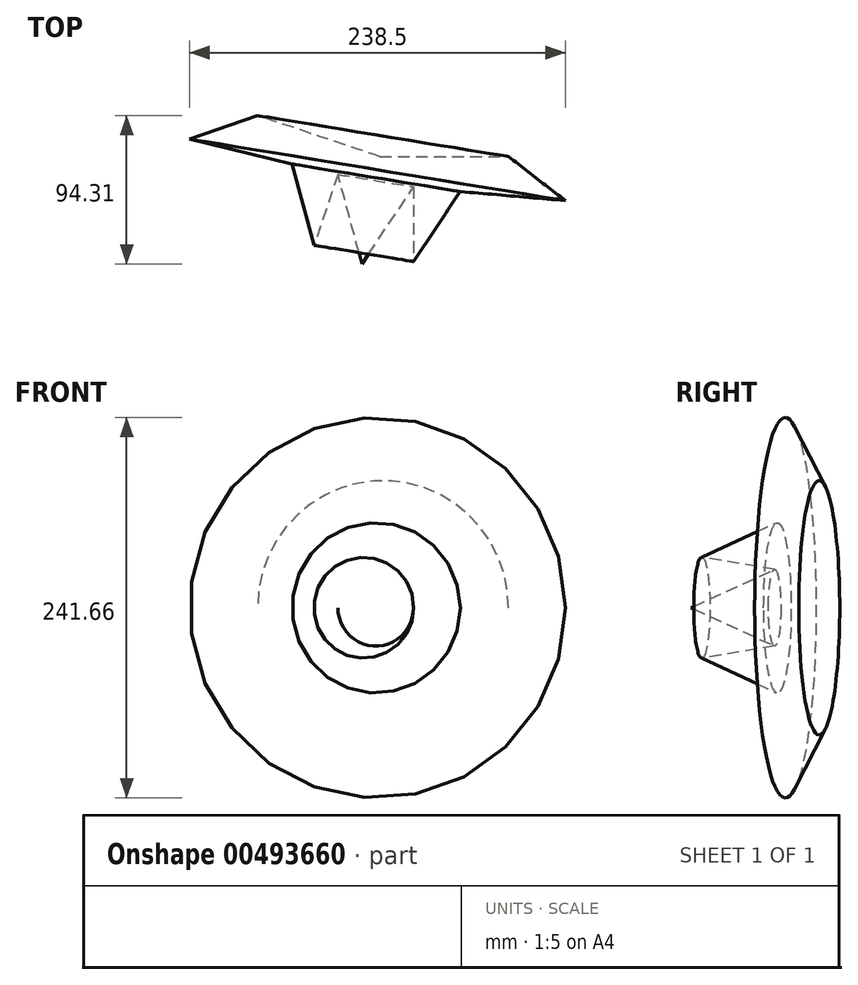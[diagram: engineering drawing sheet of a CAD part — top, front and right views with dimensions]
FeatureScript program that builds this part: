
annotation { "Feature Type Name" : "Feature", "Feature Type Description" : "" }
export const myFeature = defineFeature(function(context is Context, id is Id, definition is map)
    precondition{}
    {
        {
            var Q0;
            Q0=qCreatedBy(makeId("Top.planeOp"),FACE);
            var sketch = newSketch(context, id + "F0", { "sketchPlane" : qUnion([Q0])});
            skLineSegment(sketch, "E0", {"start": v(-38.48, 45.86) * mm, "end": v(43.35, 45.86) * mm});
            skLineSegment(sketch, "E1", {"start": v(43.35, 45.86) * mm, "end": v(79.39, 17.9) * mm});
            skLineSegment(sketch, "E2", {"start": v(79.39, 17.9) * mm, "end": v(12.7, 23.63) * mm});
            skLineSegment(sketch, "E3", {"start": v(12.7, 23.63) * mm, "end": v(-16.93, -20.82) * mm});
            skLineSegment(sketch, "E4", {"start": v(-16.93, -20.82) * mm, "end": v(-16.93, 26.66) * mm});
            skLineSegment(sketch, "E5", {"start": v(-16.93, 26.66) * mm, "end": v(-50.55, -23.77) * mm});
            skLineSegment(sketch, "E6", {"start": v(-49.93, -24.19) * mm, "end": v(-38.48, 45.86) * mm});
            skSolve(sketch);
        }
        {
            var Q0;
            {var subQ0=sQuery(id+"F0.wireOp",EDGE,"E0");Q0=makeQuery(id+"F0.imprint","IMPRINT",FACE,{"disambiguationData":[TD([[makeQuery(id+"F0.imprint","IMPRINT",EDGE,{"derivedFrom":subQ0}),-1.0]])]});}
            var Q1;
            Q1=sQuery(id+"F0.wireOp",EDGE,"E6");
            revolve(context, id + "F1", {"entities" : qUnion([Q0]), "axis" : qUnion([Q1]), "revolveType" : RevolveType.FULL});
        }
    });
